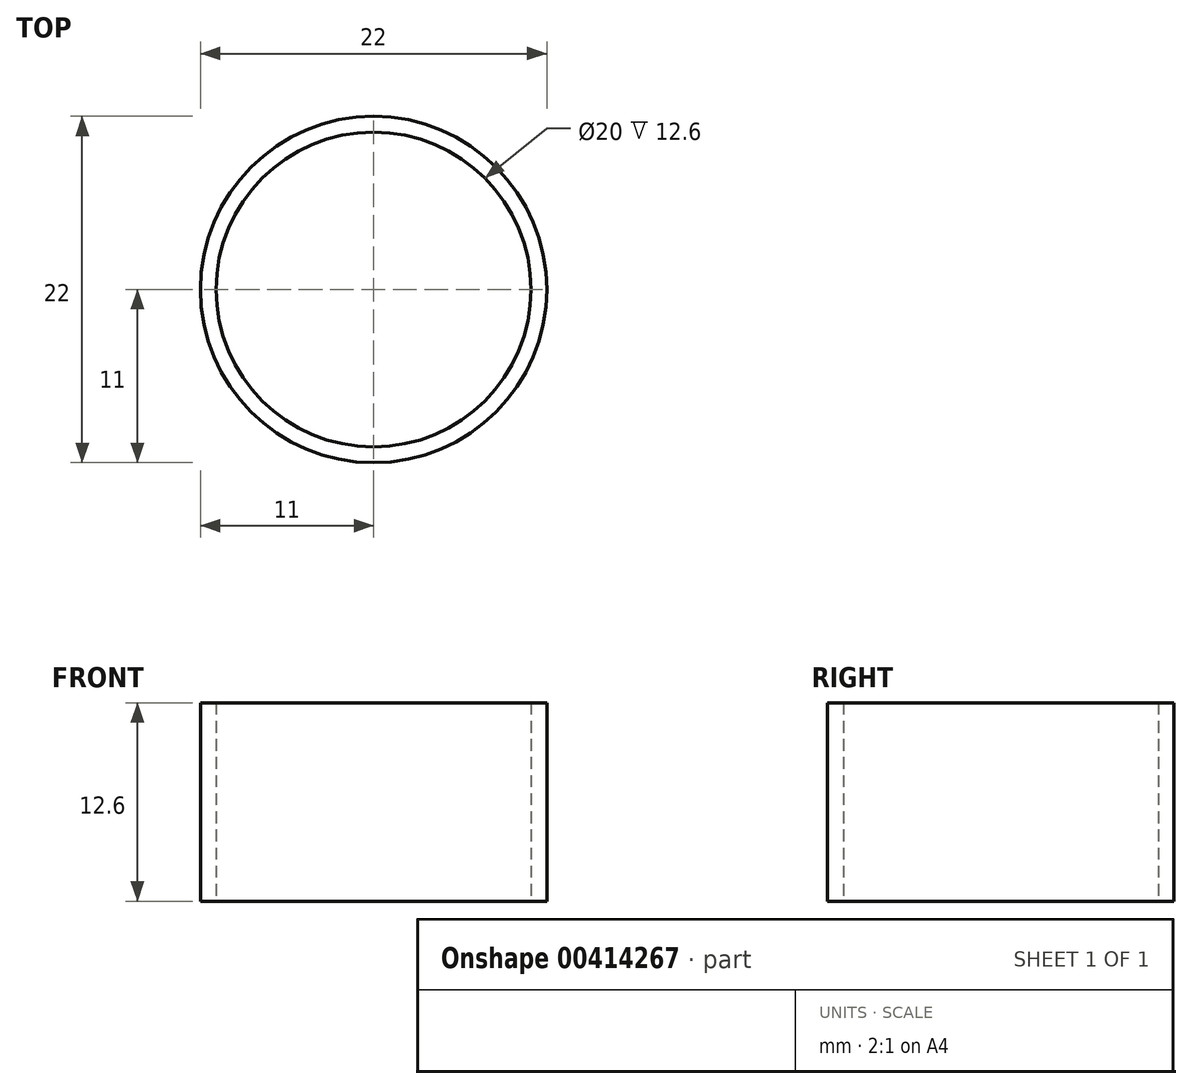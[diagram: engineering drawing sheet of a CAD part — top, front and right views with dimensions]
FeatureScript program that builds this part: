
annotation { "Feature Type Name" : "Feature", "Feature Type Description" : "" }
export const myFeature = defineFeature(function(context is Context, id is Id, definition is map)
    precondition{}
    {
        {
            var Q0;
            Q0=qCreatedBy(makeId("Top.planeOp"),FACE);
            var sketch = newSketch(context, id + "F0", { "sketchPlane" : qUnion([Q0])});
            skCircle(sketch, "E0", {"center": v(0, 0) * mm, "radius": 10 * mm});
            skCircle(sketch, "E1.0", {"center": v(0, 0) * mm, "radius": 11 * mm});
            skSolve(sketch);
        }
        {
            var Q0;
            Q0=makeQuery(id+"F0.imprint","IMPRINT",FACE,{"disambiguationData":[TD([[makeQuery(id+"F0.imprint","IMPRINT",EDGE,{"derivedFrom":sQuery(id+"F0.wireOp",EDGE,"E0")}),-1.0]])]});
            extrude(context, id + "F1", {"entities" : qUnion([Q0]), "depth" : 12.6 * mm, "offsetDistance" : 25 * mm});
        }
    });
